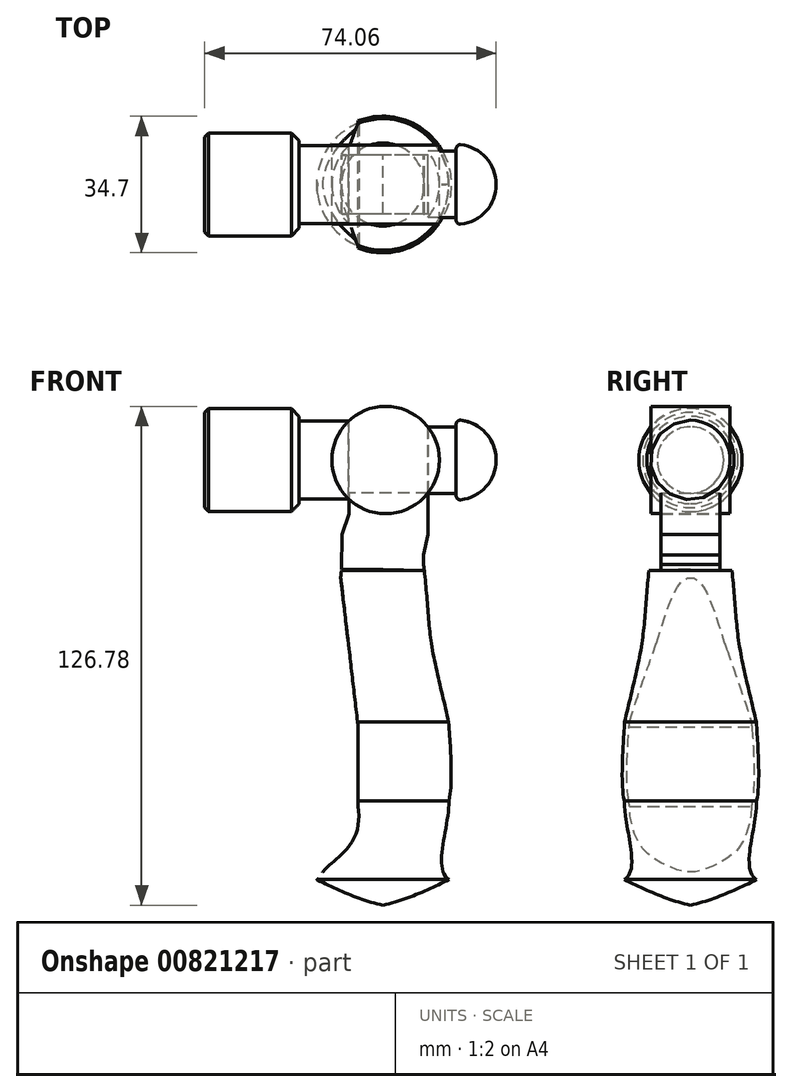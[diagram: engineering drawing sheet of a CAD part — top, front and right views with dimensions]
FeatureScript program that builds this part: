
annotation { "Feature Type Name" : "Feature", "Feature Type Description" : "" }
export const myFeature = defineFeature(function(context is Context, id is Id, definition is map)
    precondition{}
    {
        {
            var Q0;
            Q0=qCreatedBy(makeId("Front.planeOp"),FACE);
            var sketch = newSketch(context, id + "F0", { "sketchPlane" : qUnion([Q0])});
            skLineSegment(sketch, "E0.bottom", {"start": v(-32.32, 13.1) * mm, "end": v(-8.32, 13.1) * mm});
            skLineSegment(sketch, "E0.top", {"start": v(-32.32, 0) * mm, "end": v(-8.32, 0) * mm});
            skLineSegment(sketch, "E0.left", {"start": v(-32.32, 13.1) * mm, "end": v(-32.32, 0) * mm});
            skLineSegment(sketch, "E0.right", {"start": v(-8.32, 13.1) * mm, "end": v(-8.32, 0) * mm});
            skLineSegment(sketch, "E1.bottom", {"start": v(-8.32, 0) * mm, "end": v(0, 0) * mm});
            skLineSegment(sketch, "E1.top", {"start": v(-8.32, 0) * mm, "end": v(0, 0) * mm});
            skLineSegment(sketch, "E1.left", {"start": v(-8.32, 0) * mm, "end": v(-8.32, 0) * mm});
            skLineSegment(sketch, "E1.right", {"start": v(0, 0) * mm, "end": v(0, 0) * mm});
            skPoint(sketch, "E2.second.point", {"position": v(54.6, 0) * mm});
            skLineSegment(sketch, "E3", {"start": v(27.3, 0) * mm, "end": v(54.6, 0) * mm});
            skLineSegment(sketch, "E4.top", {"start": v(26.36, 0) * mm, "end": v(31.57, 0) * mm});
            skLineSegment(sketch, "E4.right", {"start": v(31.57, 8.45) * mm, "end": v(31.57, 0) * mm});
            skLineSegment(sketch, "E5", {"start": v(54.6, 0) * mm, "end": v(26.36, 0) * mm});
            skArc(sketch, "E6", {"start": v(41.74, 0) * mm, "mid": v(38.76, 7.19) * mm, "end": v(31.57, 10.16) * mm});
            skLineSegment(sketch, "E7", {"start": v(31.57, 8.45) * mm, "end": v(31.57, 10.16) * mm});
            skLineSegment(sketch, "E8", {"start": v(31.57, 0) * mm, "end": v(41.74, 0) * mm});
            skArc(sketch, "E9", {"start": v(27.3, 0) * mm, "mid": v(13.65, 13.65) * mm, "end": v(0, 0) * mm});
            skPoint(sketch, "E9.second.point", {"position": v(27.3, 0) * mm});
            skLineSegment(sketch, "E10", {"start": v(-8.32, 9.93) * mm, "end": v(4.28, 9.93) * mm});
            skLineSegment(sketch, "E11", {"start": v(31.57, 8.45) * mm, "end": v(24.37, 8.45) * mm});
            skLineSegment(sketch, "E12", {"start": v(0, 0) * mm, "end": v(27.3, 0) * mm});
            skLineSegment(sketch, "E13", {"start": v(-36.7, 0) * mm, "end": v(58.83, 0) * mm});
            skCircle(sketch, "E14", {"center": v(13.65, 0) * mm, "radius": 13.65 * mm});
            skSolve(sketch);
        }
        {
            var Q0;
            {var subQ3=sQuery(id+"F0.wireOp",EDGE,"E0.bottom");Q0=makeQuery(id+"F0.imprint","IMPRINT",FACE,{"disambiguationData":[TD([[makeQuery(id+"F0.imprint","IMPRINT",EDGE,{"derivedFrom":subQ3}),-1.0]])]});}
            var Q1;
            {var subQ0=sQuery(id+"F0.wireOp",EDGE,"E1.bottom");Q1=makeQuery(id+"F0.imprint","IMPRINT",FACE,{"disambiguationData":[TD([[makeQuery(id+"F0.imprint","IMPRINT",EDGE,{"derivedFrom":subQ0}),1.0]])]});}
            var Q2;
            {var subQ0=sQuery(id+"F0.wireOp",EDGE,"E4.right");Q2=makeQuery(id+"F0.imprint","IMPRINT",FACE,{"disambiguationData":[TD([[makeQuery(id+"F0.imprint","IMPRINT",EDGE,{"derivedFrom":subQ0}),-1.0]])]});}
            var Q3;
            {var subQ2=sQuery(id+"F0.wireOp",EDGE,"E4.right");Q3=makeQuery(id+"F0.imprint","IMPRINT",FACE,{"disambiguationData":[TD([[makeQuery(id+"F0.imprint","IMPRINT",EDGE,{"derivedFrom":subQ2}),1.0]])]});}
            var Q4;
            Q4=sQuery(id+"F0.wireOp",EDGE,"E13");
            revolve(context, id + "F1", {"surfaceOperationType" : NewSurfaceOperationType.NEW, "entities" : qUnion([Q0, Q1, Q2, Q3]), "axis" : qUnion([Q4]), "revolveType" : RevolveType.FULL});
        }
        {
            var Q0;
            {var subQ0=sQuery(id+"F0.wireOp",EDGE,"E12");var subQ1=sQuery(id+"F0.wireOp",EDGE,"E4.top");var subQ2=makeQuery(id+"F0.imprint","INTERSECT",VERTEX,{"derivedFrom":[subQ1,subQ0]});Q0=makeQuery(id+"F0.imprint","IMPRINT",FACE,{"disambiguationData":[TD([[makeQuery(id+"F0.imprint","IMPRINT",EDGE,{"disambiguationData":[TD([[subQ2,-1.0]])],"derivedFrom":subQ1}),1.0]])]});}
            var Q1;
            {var subQ0=sQuery(id+"F0.wireOp",EDGE,"E12");var subQ1=sQuery(id+"F0.wireOp",EDGE,"E4.top");var subQ2=makeQuery(id+"F0.imprint","INTERSECT",VERTEX,{"derivedFrom":[subQ1,subQ0]});Q1=makeQuery(id+"F0.imprint","IMPRINT",FACE,{"disambiguationData":[TD([[makeQuery(id+"F0.imprint","IMPRINT",EDGE,{"disambiguationData":[TD([[subQ2,-1.0]])],"derivedFrom":subQ1}),-1.0]])]});}
            extrude(context, id + "F2", {"entities" : qUnion([Q0, Q1]), "endBound" : BoundingType.SYMMETRIC, "depth" : 20 * mm, "offsetDistance" : 25 * mm});
        }
        {
            var Q0;
            Q0=makeQuery(id+"F1.opRevolve","SWEPT_EDGE",EDGE,{"disambiguationData":[OSD([sQuery(id+"F0.wireOp",EDGE,"E0.bottom"),sQuery(id+"F0.wireOp",EDGE,"E0.left")])]});
            chamfer(context, id + "F3", {"entities" : qUnion([Q0]), "width" : 1 * mm, "tangentPropagation" : true});
        }
        {
            var Q0;
            Q0=qCreatedBy(makeId("Front.planeOp"),FACE);
            var sketch = newSketch(context, id + "F4", { "sketchPlane" : qUnion([Q0])});
            skLineSegment(sketch, "E15.bottom", {"start": v(24.35, -8.42) * mm, "end": v(4.34, -8.42) * mm});
            skLineSegment(sketch, "E15.left", {"start": v(24.35, -8.42) * mm, "end": v(24.35, -18.89) * mm});
            skLineSegment(sketch, "E15.right", {"start": v(4.34, -8.42) * mm, "end": v(4.34, -13.65) * mm});
            skPoint(sketch, "E16.orphan", {"position": v(24.35, -24.49) * mm});
            skLineSegment(sketch, "E17.left", {"start": v(23.28, -24.15) * mm, "end": v(23.26, -26.6) * mm});
            skPoint(sketch, "E17.top.end.orphan", {"position": v(2.4, -30.76) * mm});
            skLineSegment(sketch, "E18", {"start": v(2.53, -18.89) * mm, "end": v(4.34, -13.65) * mm});
            skLineSegment(sketch, "E19", {"start": v(24.35, -18.89) * mm, "end": v(23.28, -24.15) * mm});
            skPoint(sketch, "E20.orphan", {"position": v(4.34, -18.89) * mm});
            skLineSegment(sketch, "E21.bottom", {"start": v(23.26, -26.6) * mm, "end": v(23.29, -26.59) * mm});
            skFitSpline(sketch, "E22", {"points": [v(23.29, -26.59) * mm, v(25.3, -46.59) * mm], "startDerivative": vector(2.67, -19.39) * mm, "endDerivative": vector(2.86, -18.03) * mm});
            skFitSpline(sketch, "E23", {"points": [v(25.3, -46.59) * mm, v(29.66, -66.59) * mm], "startDerivative": vector(2.95, -19.1) * mm, "endDerivative": vector(4.53, -20.46) * mm});
            skFitSpline(sketch, "E24", {"points": [v(29.66, -66.59) * mm, v(29.73, -86.59) * mm], "startDerivative": vector(1.3, -17.49) * mm, "endDerivative": vector(-3.2, -11.42) * mm});
            skFitSpline(sketch, "E25", {"points": [v(29.73, -86.59) * mm, v(29.73, -106.59) * mm], "startDerivative": vector(0.32, -20.52) * mm, "endDerivative": vector(12.84, -7.7) * mm});
            skFitSpline(sketch, "E26", {"points": [v(-7.81, -110.83) * mm, v(29.73, -106.59) * mm], "startDerivative": vector(37.94, -21.72) * mm, "endDerivative": vector(31.25, 15.64) * mm});
            skLineSegment(sketch, "E27", {"start": v(12.95, -27.77) * mm, "end": v(12.95, -113.13) * mm});
            skPoint(sketch, "E28.0.internal.orphan", {"position": v(6.67, -67.66) * mm});
            skPoint(sketch, "E28.1.internal.orphan", {"position": v(6.67, -87.66) * mm});
            skPoint(sketch, "E29.end.orphan", {"position": v(4.23, -47.66) * mm});
            skLineSegment(sketch, "E30", {"start": v(6.67, -87.66) * mm, "end": v(12.95, -87.22) * mm});
            skLineSegment(sketch, "E31", {"start": v(23.48, -28.09) * mm, "end": v(12.95, -27.77) * mm});
            skLineSegment(sketch, "E32", {"start": v(2.53, -18.89) * mm, "end": v(2.4, -30.76) * mm});
            skLineSegment(sketch, "E33", {"start": v(4.23, -47.66) * mm, "end": v(2.4, -30.76) * mm});
            skLineSegment(sketch, "E34", {"start": v(4.23, -47.66) * mm, "end": v(6.67, -67.66) * mm});
            skLineSegment(sketch, "E35", {"start": v(6.67, -67.66) * mm, "end": v(6.67, -87.66) * mm});
            skLineSegment(sketch, "E36", {"start": v(12.95, -27.77) * mm, "end": v(2.4, -27.77) * mm});
            skFitSpline(sketch, "E37", {"points": [v(6.67, -87.66) * mm, v(-7.81, -110.83) * mm], "startDerivative": vector(2.46, -39.95) * mm, "endDerivative": vector(-14.48, -23.16) * mm});
            skSolve(sketch);
        }
        {
            var Q0;
            Q0=makeQuery(id+"F1.opRevolve","SWEPT_EDGE",EDGE,{"disambiguationData":[OSD([sQuery(id+"F0.wireOp",EDGE,"E0.bottom"),sQuery(id+"F0.wireOp",EDGE,"E0.right")])]});
            chamfer(context, id + "F5", {"entities" : qUnion([Q0]), "width" : 2 * mm, "tangentPropagation" : true});
        }
        {
            var Q0;
            Q0=makeQuery(id+"F1.opRevolve","SWEPT_EDGE",EDGE,{"disambiguationData":[OSD([sQuery(id+"F0.wireOp",EDGE,"E6"),sQuery(id+"F0.wireOp",EDGE,"E7")])]});
            fillet(context, id + "F6", {"entities" : qUnion([Q0]), "radius" : 1 * mm, "tangentPropagation" : true, "allowEdgeOverflow" : false});
        }
        {
            var Q0;
            {var subQ1=sQuery(id+"F4.wireOp",EDGE,"E23");Q0=makeQuery(id+"F4.imprint","IMPRINT",FACE,{"disambiguationData":[TD([[makeQuery(id+"F4.imprint","IMPRINT",EDGE,{"derivedFrom":subQ1}),-1.0]])]});}
            var Q1;
            Q1=sQuery(id+"F4.wireOp",EDGE,"E27");
            revolve(context, id + "F7", {"surfaceOperationType" : NewSurfaceOperationType.NEW, "entities" : qUnion([Q0]), "axis" : qUnion([Q1]), "revolveType" : RevolveType.SYMMETRIC, "angle" : 360 * degree});
        }
        {
            var Q0;
            Q0=makeQuery(id+"F4.imprint","IMPRINT",FACE,{"disambiguationData":[TD([[makeQuery(id+"F4.imprint","IMPRINT",EDGE,{"derivedFrom":sQuery(id+"F4.wireOp",EDGE,"E15.bottom")}),1.0]])]});
            extrude(context, id + "F8", {"entities" : qUnion([Q0]), "endBound" : BoundingType.SYMMETRIC, "depth" : 15 * mm, "offsetDistance" : 25 * mm});
        }
        {
            var Q0;
            Q0=qCreatedBy(makeId("Front.planeOp"),FACE);
            var sketch = newSketch(context, id + "F9", { "sketchPlane" : qUnion([Q0])});
            skLineSegment(sketch, "E38", {"start": v(2.04, -28.3) * mm, "end": v(4.35, -48) * mm});
            skLineSegment(sketch, "E39", {"start": v(4.35, -48) * mm, "end": v(6.68, -67.85) * mm});
            skLineSegment(sketch, "E40", {"start": v(6.68, -67.85) * mm, "end": v(6.68, -87.96) * mm});
            skFitSpline(sketch, "E41", {"points": [v(6.68, -87.96) * mm, v(-3.74, -106.7) * mm], "startDerivative": vector(4.25, -34.99) * mm, "endDerivative": vector(-10.42, -18.73) * mm});
            skLineSegment(sketch, "E42", {"start": v(2.04, -28.3) * mm, "end": v(-6.07, -69.2) * mm});
            skLineSegment(sketch, "E43", {"start": v(-6.07, -69.2) * mm, "end": v(-3.74, -106.7) * mm});
            skSolve(sketch);
        }
        {
            var Q0;
            Q0=makeQuery(id+"F9.imprint","IMPRINT",FACE,{"disambiguationData":[TD([[makeQuery(id+"F9.imprint","IMPRINT",EDGE,{"derivedFrom":sQuery(id+"F9.wireOp",EDGE,"E38")}),-1.0]])]});
            extrude(context, id + "F10", {"entities" : qUnion([Q0]), "operationType" : NewBodyOperationType.REMOVE, "endBound" : BoundingType.SYMMETRIC, "depth" : 500 * mm, "offsetDistance" : 25 * mm});
        }
    });
